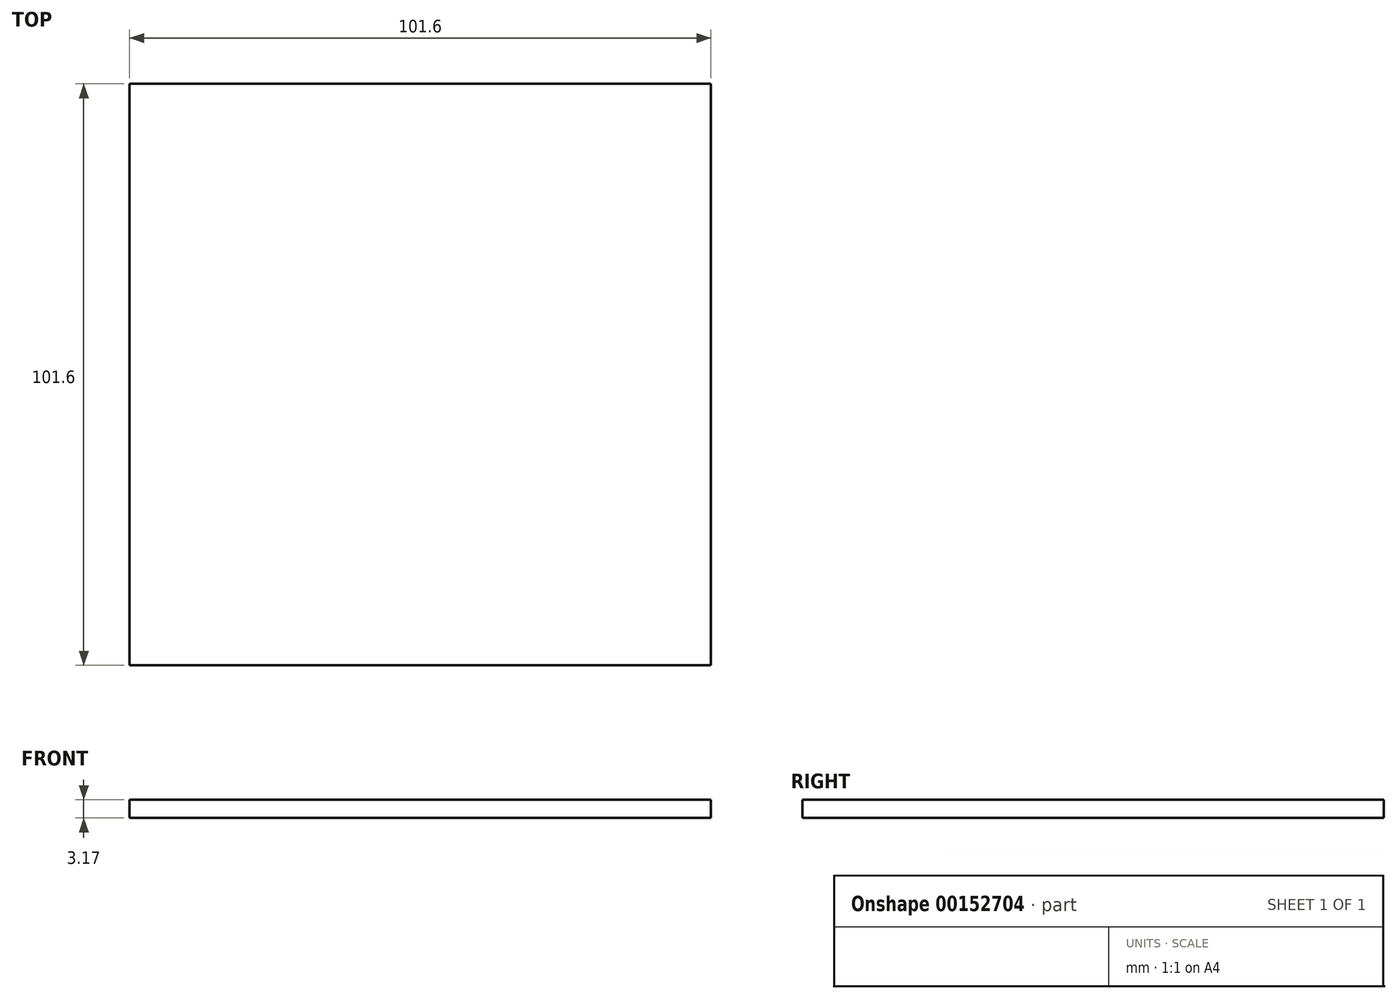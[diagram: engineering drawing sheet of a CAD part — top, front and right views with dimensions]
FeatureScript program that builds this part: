
annotation { "Feature Type Name" : "Feature", "Feature Type Description" : "" }
export const myFeature = defineFeature(function(context is Context, id is Id, definition is map)
    precondition{}
    {
        {
            var Q0;
            Q0=qCreatedBy(makeId("Top.planeOp"),FACE);
            var sketch = newSketch(context, id + "F0", { "sketchPlane" : qUnion([Q0])});
            skLineSegment(sketch, "E0.bottom", {"start": v(0, 0) * mm, "end": v(101.6, 0) * mm});
            skLineSegment(sketch, "E0.top", {"start": v(0, -101.6) * mm, "end": v(101.6, -101.6) * mm});
            skLineSegment(sketch, "E0.left", {"start": v(0, 0) * mm, "end": v(0, -101.6) * mm});
            skLineSegment(sketch, "E0.right", {"start": v(101.6, 0) * mm, "end": v(101.6, -101.6) * mm});
            skSolve(sketch);
        }
        {
            var Q0;
            Q0 = qSketchRegion(id + "F0", true);
            extrude(context, id + "F1", {"entities" : qUnion([Q0]), "depth" : 3.17 * mm});
        }
    });
